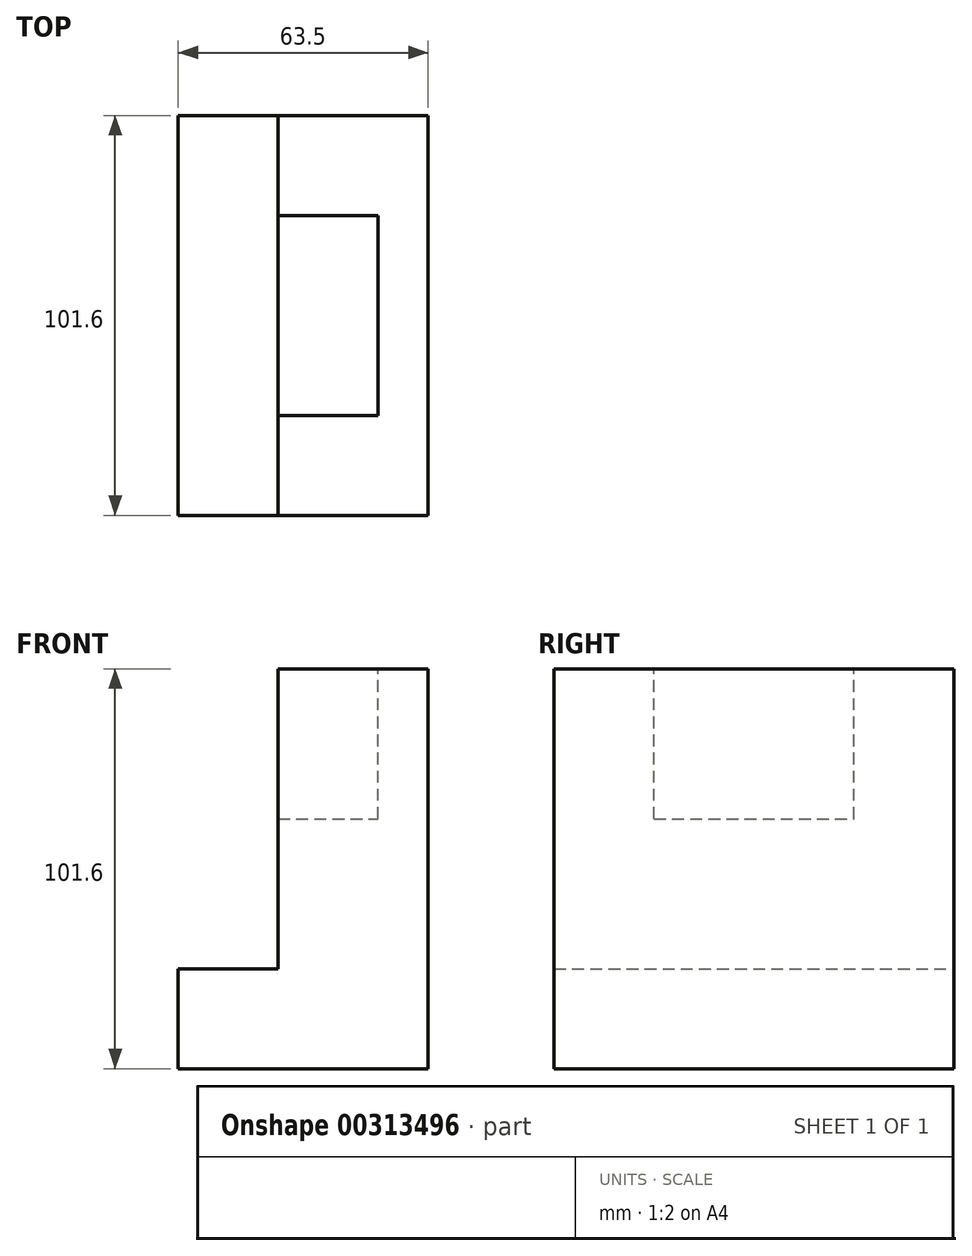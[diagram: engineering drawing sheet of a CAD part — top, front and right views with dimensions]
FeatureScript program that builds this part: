
annotation { "Feature Type Name" : "Feature", "Feature Type Description" : "" }
export const myFeature = defineFeature(function(context is Context, id is Id, definition is map)
    precondition{}
    {
        {
            var Q0;
            Q0=qCreatedBy(makeId("Front.planeOp"),FACE);
            var sketch = newSketch(context, id + "F0", { "sketchPlane" : qUnion([Q0])});
            skLineSegment(sketch, "E0", {"start": v(-40.34, -41.63) * mm, "end": v(23.16, -41.63) * mm});
            skLineSegment(sketch, "E1", {"start": v(23.16, -41.63) * mm, "end": v(23.16, 34.57) * mm});
            skLineSegment(sketch, "E2", {"start": v(23.16, 34.57) * mm, "end": v(-14.94, 34.57) * mm});
            skLineSegment(sketch, "E3", {"start": v(-14.94, 34.57) * mm, "end": v(-14.94, -16.23) * mm});
            skLineSegment(sketch, "E4", {"start": v(-14.94, -16.23) * mm, "end": v(-40.34, -16.23) * mm});
            skLineSegment(sketch, "E5", {"start": v(-40.34, -16.23) * mm, "end": v(-40.34, -41.63) * mm});
            skSolve(sketch);
        }
        {
            var Q0;
            Q0=makeQuery(id+"F0.imprint","IMPRINT",FACE,{"disambiguationData":[TD([[makeQuery(id+"F0.imprint","IMPRINT",EDGE,{"derivedFrom":sQuery(id+"F0.wireOp",EDGE,"E0")}),1.0]])]});
            extrude(context, id + "F1", {"entities" : qUnion([Q0]), "depth" : 101.6 * mm});
        }
        {
            var Q0;
            Q0=makeQuery(id+"F1.opExtrude","SWEPT_FACE",FACE,{"disambiguationData":[OSD([sQuery(id+"F0.wireOp",EDGE,"E2")])]});
            extrude(context, id + "F2", {"entities" : qUnion([Q0]), "operationType" : NewBodyOperationType.ADD, "depth" : 25.4 * mm});
        }
        {
            var Q0;
            Q0=makeQuery(id+"F2.opExtrude","CAP_FACE",FACE,{"disambiguationData":[OSD([sQuery(id+"F0.wireOp",EDGE,"E2")])],"isStart":false});
            var sketch = newSketch(context, id + "F3", { "sketchPlane" : qUnion([Q0])});
            skLineSegment(sketch, "E6", {"start": v(-14.94, 0) * mm, "end": v(-14.94, -25.45) * mm});
            skLineSegment(sketch, "E7", {"start": v(-14.94, -25.45) * mm, "end": v(10.46, -25.45) * mm});
            skLineSegment(sketch, "E8", {"start": v(-14.94, -101.6) * mm, "end": v(-14.94, -76.2) * mm});
            skLineSegment(sketch, "E9", {"start": v(-14.94, -76.2) * mm, "end": v(10.46, -76.2) * mm});
            skLineSegment(sketch, "E10", {"start": v(10.46, -25.45) * mm, "end": v(10.46, -76.2) * mm});
            skSolve(sketch);
        }
        {
            var Q0;
            {var subQ0=sQuery(id+"F3.wireOp",EDGE,"E7");Q0=makeQuery(id+"F3.imprint","IMPRINT",FACE,{"disambiguationData":[TD([[makeQuery(id+"F3.imprint","IMPRINT",EDGE,{"derivedFrom":subQ0}),-1.0]])]});}
            extrude(context, id + "F4", {"entities" : qUnion([Q0]), "operationType" : NewBodyOperationType.REMOVE, "depth" : -38.1 * mm});
        }
    });
